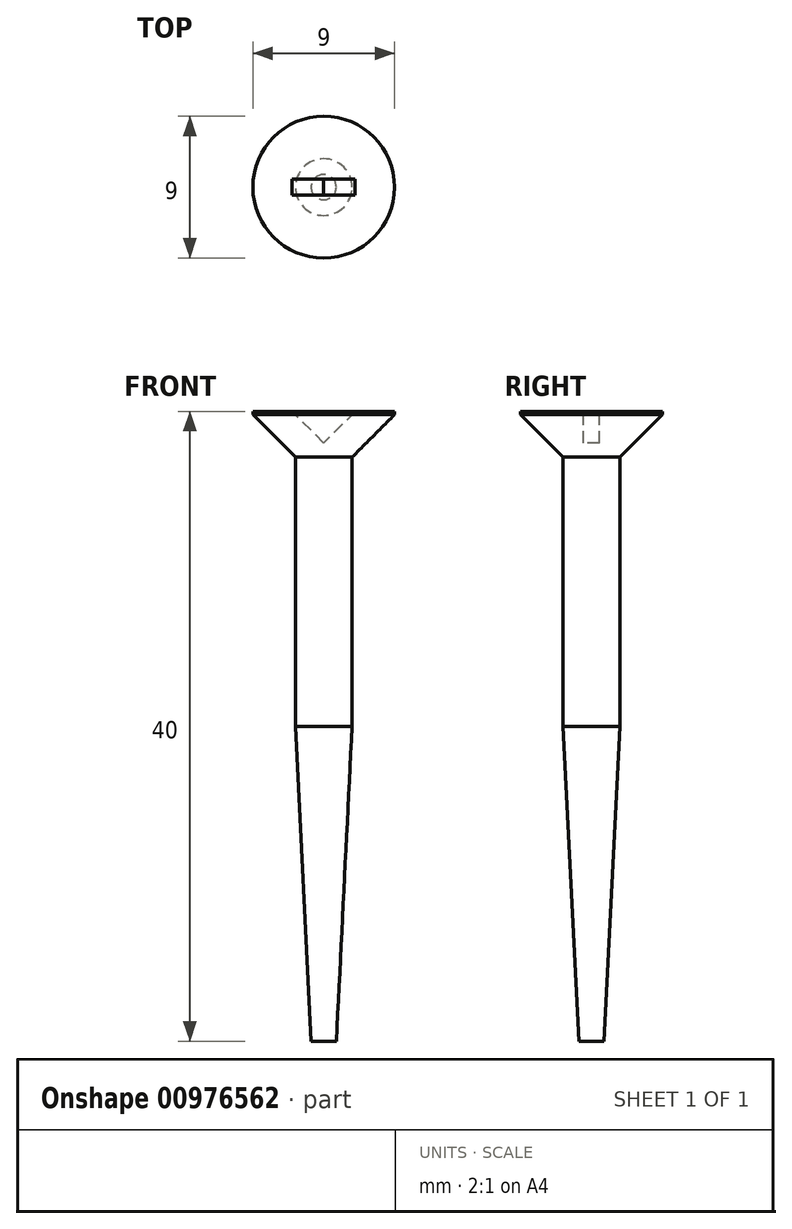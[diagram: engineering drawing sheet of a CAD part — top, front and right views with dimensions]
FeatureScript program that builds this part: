
annotation { "Feature Type Name" : "Feature", "Feature Type Description" : "" }
export const myFeature = defineFeature(function(context is Context, id is Id, definition is map)
    precondition{}
    {
        {
            var Q0;
            Q0=qCreatedBy(makeId("Front.planeOp"),FACE);
            var sketch = newSketch(context, id + "F0", { "sketchPlane" : qUnion([Q0])});
            skLineSegment(sketch, "E0", {"start": v(0, 0) * mm, "end": v(0, -40) * mm});
            skLineSegment(sketch, "E1", {"start": v(0, -40) * mm, "end": v(-1.8, -40) * mm});
            skLineSegment(sketch, "E2", {"start": v(-1.8, -40) * mm, "end": v(-1.8, -2.9) * mm});
            skLineSegment(sketch, "E3", {"start": v(-1.8, -2.9) * mm, "end": v(-4.5, -0.2) * mm});
            skLineSegment(sketch, "E4", {"start": v(-4.5, -0.2) * mm, "end": v(-4.5, 0) * mm});
            skLineSegment(sketch, "E5", {"start": v(-4.5, 0) * mm, "end": v(0, 0) * mm});
            skSolve(sketch);
        }
        {
            var Q0;
            Q0=makeQuery(id+"F0.imprint","IMPRINT",FACE,{"disambiguationData":[TD([[makeQuery(id+"F0.imprint","IMPRINT",EDGE,{"derivedFrom":sQuery(id+"F0.wireOp",EDGE,"E0")}),-1.0]])]});
            var Q1;
            Q1=sQuery(id+"F0.wireOp",EDGE,"E0");
            revolve(context, id + "F1", {"surfaceOperationType" : NewSurfaceOperationType.NEW, "entities" : qUnion([Q0]), "axis" : qUnion([Q1]), "revolveType" : RevolveType.FULL});
        }
        {
            var Q0;
            Q0=makeQuery(id+"F1.opRevolve","SWEPT_EDGE",EDGE,{"disambiguationData":[OSD([sQuery(id+"F0.wireOp",EDGE,"E1"),sQuery(id+"F0.wireOp",EDGE,"E2")])]});
            chamfer(context, id + "F2", {"entities" : qUnion([Q0]), "chamferType" : ChamferType.TWO_OFFSETS, "width1" : 20 * mm, "oppositeDirection" : false, "width2" : 1 * mm, "tangentPropagation" : true});
        }
        {
            var Q0;
            Q0=qCreatedBy(makeId("Front.planeOp"),FACE);
            var sketch = newSketch(context, id + "F3", { "sketchPlane" : qUnion([Q0])});
            skLineSegment(sketch, "E6", {"start": v(-2, 0) * mm, "end": v(2, 0) * mm});
            skLineSegment(sketch, "E7", {"start": v(2, 0) * mm, "end": v(0, -2) * mm});
            skLineSegment(sketch, "E8", {"start": v(0, -2) * mm, "end": v(-2, 0) * mm});
            skSolve(sketch);
        }
        {
            var Q0;
            Q0 = qSketchRegion(id + "F3", true);
            extrude(context, id + "F4", {"entities" : qUnion([Q0]), "operationType" : NewBodyOperationType.REMOVE, "endBound" : BoundingType.SYMMETRIC, "oppositeDirection" : true, "depth" : 1 * mm, "offsetDistance" : 25 * mm});
        }
    });
